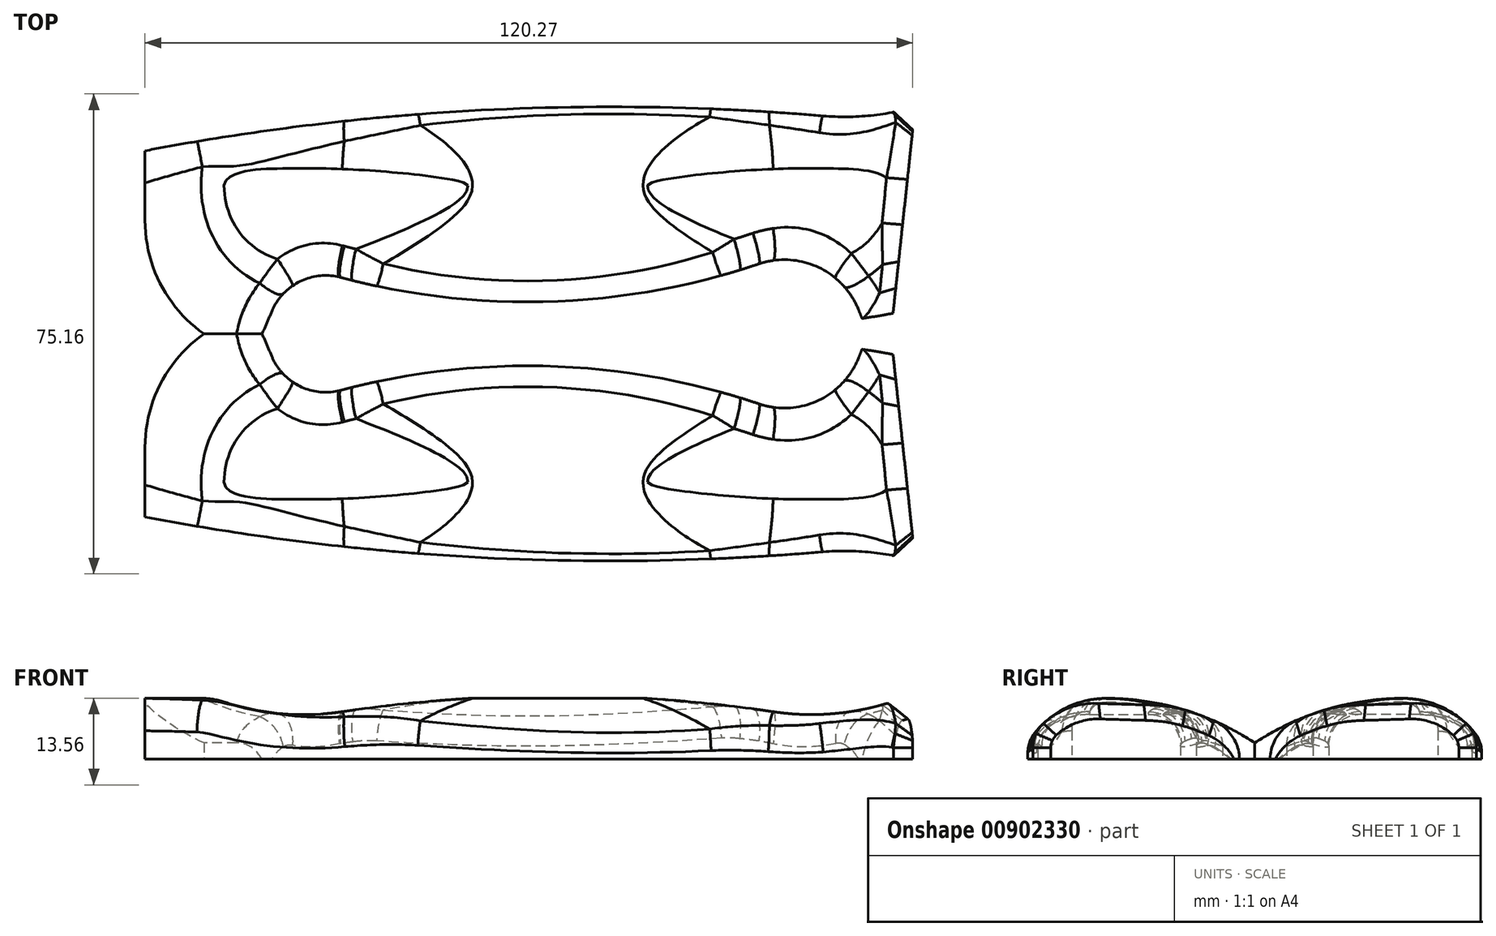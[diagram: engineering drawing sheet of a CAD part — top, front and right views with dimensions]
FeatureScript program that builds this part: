
annotation { "Feature Type Name" : "Feature", "Feature Type Description" : "" }
export const myFeature = defineFeature(function(context is Context, id is Id, definition is map)
    precondition{}
    {
        {
            var Q0;
            Q0=qCreatedBy(makeId("Top.planeOp"),FACE);
            var sketch = newSketch(context, id + "F0", { "sketchPlane" : qUnion([Q0])});
            skLineSegment(sketch, "E0", {"start": v(0, 35.56) * mm, "end": v(0, 0) * mm, "construction": true});
            skLineSegment(sketch, "E1", {"start": v(0, 0) * mm, "end": v(116.84, 0) * mm, "construction": true});
            skLineSegment(sketch, "E2", {"start": v(116.84, 0) * mm, "end": v(120.65, 35.56) * mm, "construction": true});
            skLineSegment(sketch, "E3", {"start": v(120.65, 35.56) * mm, "end": v(0, 35.56) * mm, "construction": true});
            skSolve(sketch);
        }
        {
            var Q0;
            Q0=qCreatedBy(makeId("Top.planeOp"),FACE);
            var sketch = newSketch(context, id + "F1", { "sketchPlane" : qUnion([Q0])});
            skLineSegment(sketch, "E4.0", {"start": v(120.65, 35.56) * mm, "end": v(0, 35.56) * mm, "construction": true});
            skLineSegment(sketch, "E5.0", {"start": v(0, 35.56) * mm, "end": v(0, 0) * mm, "construction": true});
            skLineSegment(sketch, "E6.0", {"start": v(0, 0) * mm, "end": v(116.84, 0) * mm, "construction": true});
            skLineSegment(sketch, "E7.0", {"start": v(116.84, 0) * mm, "end": v(120.65, 35.56) * mm, "construction": true});
            skArc(sketch, "E8", {"start": v(120.34, 32.66) * mm, "mid": v(113.28, 33.46) * mm, "end": v(106.21, 34.14) * mm, "construction": true});
            skArc(sketch, "E9", {"start": v(0, 17.78) * mm, "mid": v(2.44, 7.76) * mm, "end": v(9.23, 0) * mm});
            skLineSegment(sketch, "E10", {"start": v(0, 28.68) * mm, "end": v(0, 17.78) * mm});
            skArc(sketch, "E11", {"start": v(106.21, 34.14) * mm, "mid": v(113.5, 34.18) * mm, "end": v(120.65, 35.56) * mm});
            skArc(sketch, "E12", {"start": v(30.65, 8.84) * mm, "mid": v(22.72, 7.25) * mm, "end": v(19.15, 0) * mm});
            skArc(sketch, "E13", {"start": v(30.65, 8.84) * mm, "mid": v(63.56, 5.06) * mm, "end": v(96.16, 10.96) * mm});
            skArc(sketch, "E14", {"start": v(106.21, 34.14) * mm, "mid": v(52.92, 35.05) * mm, "end": v(0, 28.68) * mm});
            skLineSegment(sketch, "E15", {"start": v(120.65, 35.56) * mm, "end": v(116.84, 0) * mm});
            skLineSegment(sketch, "E16", {"start": v(112.65, 0) * mm, "end": v(116.84, 0) * mm});
            skArc(sketch, "E17", {"start": v(112.65, 0) * mm, "mid": v(107.1, 9.52) * mm, "end": v(96.16, 10.96) * mm});
            skLineSegment(sketch, "E18", {"start": v(9.23, 0) * mm, "end": v(19.15, 0) * mm});
            skSolve(sketch);
        }
        {
            var Q0;
            Q0 = qSketchRegion(id + "F1", true);
            extrude(context, id + "F2", {"entities" : qUnion([Q0]), "depth" : 12.7 * mm, "offsetDistance" : 25.4 * mm});
        }
        {
            var Q0;
            Q0=qCreatedBy(makeId("Right.planeOp"),FACE);
            var sketch = newSketch(context, id + "F3", { "sketchPlane" : qUnion([Q0])});
            skLineSegment(sketch, "E19.0", {"start": v(35.56, 0) * mm, "end": v(0, 0) * mm, "construction": true});
            skLineSegment(sketch, "E20", {"start": v(35.56, 0) * mm, "end": v(35.56, 2.54) * mm, "construction": true});
            skLineSegment(sketch, "E21", {"start": v(35.56, 2.54) * mm, "end": v(35.56, 2.54) * mm});
            skLineSegment(sketch, "E22", {"start": v(0, 2.54) * mm, "end": v(0, 0) * mm, "construction": true});
            skLineSegment(sketch, "E23", {"start": v(23.23, 12.7) * mm, "end": v(23.23, -4.85) * mm, "construction": true});
            skLineSegment(sketch, "E24", {"start": v(17.78, 12.7) * mm, "end": v(17.78, -21.71) * mm, "construction": true});
            skArc(sketch, "E25", {"start": v(23.23, 9.52) * mm, "mid": v(11.1, 7.74) * mm, "end": v(0, 2.54) * mm});
            skArc(sketch, "E26", {"start": v(0, 2.54) * mm, "mid": v(35.36, -72.92) * mm, "end": v(23.23, 9.52) * mm, "construction": true});
            skLineSegment(sketch, "E27", {"start": v(35.56, 2.54) * mm, "end": v(0, 2.54) * mm, "construction": true});
            skArc(sketch, "E28", {"start": v(23.23, 9.53) * mm, "mid": v(16.14, -17.36) * mm, "end": v(35.56, 2.54) * mm, "construction": true});
            skArc(sketch, "E29", {"start": v(35.56, 2.54) * mm, "mid": v(30.31, 7.66) * mm, "end": v(23.23, 9.53) * mm});
            skLineSegment(sketch, "E30.0", {"start": v(35.56, 12.7) * mm, "end": v(0, 12.7) * mm});
            skLineSegment(sketch, "E31", {"start": v(35.56, 2.54) * mm, "end": v(35.56, 12.7) * mm});
            skLineSegment(sketch, "E32", {"start": v(0, 12.7) * mm, "end": v(0, 2.54) * mm});
            skSolve(sketch);
        }
        {
            var Q0;
            Q0 = qSketchRegion(id + "F3", true);
            extrude(context, id + "F4", {"entities" : qUnion([Q0]), "operationType" : NewBodyOperationType.REMOVE, "endBound" : BoundingType.THROUGH_ALL, "depth" : 254 * mm, "offsetDistance" : 25.4 * mm});
        }
        {
            var Q0;
            Q0=qCreatedBy(makeId("Front.planeOp"),FACE);
            var sketch = newSketch(context, id + "F5", { "sketchPlane" : qUnion([Q0])});
            skLineSegment(sketch, "E33.0", {"start": v(30.65, 0) * mm, "end": v(19.15, 0) * mm, "construction": true});
            skLineSegment(sketch, "E34.0", {"start": v(112.65, 0) * mm, "end": v(96.16, 0) * mm, "construction": true});
            skLineSegment(sketch, "E35", {"start": v(24.9, 47.63) * mm, "end": v(24.9, 0) * mm, "construction": true});
            skLineSegment(sketch, "E36", {"start": v(104.4, 0) * mm, "end": v(104.4, 47.62) * mm, "construction": true});
            skLineSegment(sketch, "E37.0", {"start": v(119.33, 9.52) * mm, "end": v(118.55, 9.52) * mm});
            skArc(sketch, "E38", {"start": v(98.4, 7.43) * mm, "mid": v(64.65, 9.94) * mm, "end": v(30.9, 7.43) * mm});
            skArc(sketch, "E39", {"start": v(30.9, 7.43) * mm, "mid": v(61.28, -447.24) * mm, "end": v(105.07, 6.34) * mm, "construction": true});
            skArc(sketch, "E40", {"start": v(105.07, 6.34) * mm, "mid": v(101.74, 6.9) * mm, "end": v(98.4, 7.43) * mm});
            skLineSegment(sketch, "E41", {"start": v(118.55, 9.53) * mm, "end": v(10.76, 9.53) * mm, "construction": true});
            skLineSegment(sketch, "E42", {"start": v(119.33, 9.53) * mm, "end": v(10.76, 9.53) * mm});
            skArc(sketch, "E43", {"start": v(10.76, 9.53) * mm, "mid": v(20.7, 7.2) * mm, "end": v(30.9, 7.43) * mm});
            skArc(sketch, "E44", {"start": v(30.9, 7.43) * mm, "mid": v(29.1, 88.05) * mm, "end": v(10.76, 9.53) * mm, "construction": true});
            skArc(sketch, "E45", {"start": v(118.55, 9.52) * mm, "mid": v(100.2, 88.05) * mm, "end": v(98.4, 7.43) * mm, "construction": true});
            skArc(sketch, "E46", {"start": v(98.4, 7.43) * mm, "mid": v(108.61, 7.2) * mm, "end": v(118.55, 9.52) * mm});
            skLineSegment(sketch, "E47", {"start": v(119.33, 9.52) * mm, "end": v(119.33, 47.62) * mm});
            skLineSegment(sketch, "E48", {"start": v(119.33, 47.62) * mm, "end": v(119.33, 47.62) * mm});
            skSolve(sketch);
        }
        {
            var Q0;
            Q0 = qSketchRegion(id + "F5", true);
            extrude(context, id + "F6", {"entities" : qUnion([Q0]), "operationType" : NewBodyOperationType.REMOVE, "endBound" : BoundingType.THROUGH_ALL, "oppositeDirection" : true, "depth" : 101.6 * mm, "offsetDistance" : 25.4 * mm});
        }
        {
            var Q0;
            Q0=makeQuery(id+"F6.boolean.opBoolean","INTERSECT",EDGE,{"disambiguationData":[OD(1.0)],"derivedFrom":[makeQuery(id+"F4.boolean.opBoolean","COPY",FACE,{"derivedFrom":makeQuery(id+"F4.opExtrude","SWEPT_FACE",FACE,{"disambiguationData":[OSD([sQuery(id+"F3.wireOp",EDGE,"E25")])]})}),makeQuery(id+"F6.opExtrude","SWEPT_FACE",FACE,{"disambiguationData":[OSD([sQuery(id+"F5.wireOp",EDGE,"E43")])]})]});
            var Q1;
            Q1=makeQuery(id+"F6.boolean.opBoolean","INTERSECT",EDGE,{"disambiguationData":[OD(1.0)],"derivedFrom":[makeQuery(id+"F4.boolean.opBoolean","COPY",FACE,{"derivedFrom":makeQuery(id+"F4.opExtrude","SWEPT_FACE",FACE,{"disambiguationData":[OSD([sQuery(id+"F3.wireOp",EDGE,"E25")])]})}),makeQuery(id+"F6.opExtrude","SWEPT_FACE",FACE,{"disambiguationData":[OSD([sQuery(id+"F5.wireOp",EDGE,"E38")])]})]});
            fillet(context, id + "F7", {"entities" : qUnion([Q0, Q1]), "radius" : 11.68 * mm, "tangentPropagation" : true, "allowEdgeOverflow" : false});
        }
        {
            var Q0;
            Q0=makeQuery(id+"F4.boolean.opBoolean","INTERSECT",EDGE,{"derivedFrom":[makeQuery(id+"F2.opExtrude","SWEPT_FACE",FACE,{"disambiguationData":[OSD([sQuery(id+"F1.wireOp",EDGE,"E13")])]}),makeQuery(id+"F4.opExtrude","SWEPT_FACE",FACE,{"disambiguationData":[OSD([sQuery(id+"F3.wireOp",EDGE,"E25")])]})]});
            var Q1;
            Q1=makeQuery(id+"F4.boolean.opBoolean","INTERSECT",EDGE,{"derivedFrom":[makeQuery(id+"F2.opExtrude","SWEPT_FACE",FACE,{"disambiguationData":[OSD([sQuery(id+"F1.wireOp",EDGE,"E14")])]}),makeQuery(id+"F4.opExtrude","SWEPT_FACE",FACE,{"disambiguationData":[OSD([sQuery(id+"F3.wireOp",EDGE,"E29")])]})]});
            fillet(context, id + "F8", {"entities" : qUnion([Q0, Q1]), "radius" : 5.08 * mm, "tangentPropagation" : true, "allowEdgeOverflow" : false});
        }
        {
            var Q0;
            Q0=makeQuery(id+"F4.boolean.opBoolean","INTERSECT",EDGE,{"derivedFrom":[makeQuery(id+"F2.opExtrude","SWEPT_FACE",FACE,{"disambiguationData":[OSD([sQuery(id+"F1.wireOp",EDGE,"E15")])]}),makeQuery(id+"F4.opExtrude","SWEPT_FACE",FACE,{"disambiguationData":[OSD([sQuery(id+"F3.wireOp",EDGE,"E25")])]})]});
            var Q1;
            Q1=makeQuery(id+"F7.opFillet","BLEND_EDGE",EDGE,{"blendedFrom":[makeQuery(id+"F6.boolean.opBoolean","INTERSECT",EDGE,{"derivedFrom":[makeQuery(id+"F4.boolean.opBoolean","COPY",FACE,{"derivedFrom":makeQuery(id+"F4.opExtrude","SWEPT_FACE",FACE,{"disambiguationData":[OSD([sQuery(id+"F3.wireOp",EDGE,"E25")])]})}),makeQuery(id+"F6.opExtrude","SWEPT_FACE",FACE,{"disambiguationData":[OSD([sQuery(id+"F5.wireOp",EDGE,"E46")])]})]}),makeQuery(id+"F2.opExtrude","SWEPT_FACE",FACE,{"disambiguationData":[OSD([sQuery(id+"F1.wireOp",EDGE,"E15")])]})],"blendedInto":[makeQuery(id+"F2.opExtrude","SWEPT_FACE",FACE,{"disambiguationData":[OSD([sQuery(id+"F1.wireOp",EDGE,"E15")])]})]});
            chamfer(context, id + "F9", {"entities" : qUnion([Q0, Q1]), "width" : 2.54 * mm, "tangentPropagation" : true});
        }
        {
            var Q0;
            Q0=makeQuery(id+"F2.opExtrude","SWEPT_BODY",BODY,{"disambiguationData":[OSD([sQuery(id+"F1.wireOp",EDGE,"E9"),sQuery(id+"F1.wireOp",EDGE,"E10"),sQuery(id+"F1.wireOp",EDGE,"E11"),sQuery(id+"F1.wireOp",EDGE,"E12"),sQuery(id+"F1.wireOp",EDGE,"E13"),sQuery(id+"F1.wireOp",EDGE,"E14"),sQuery(id+"F1.wireOp",EDGE,"E15"),sQuery(id+"F1.wireOp",EDGE,"E16"),sQuery(id+"F1.wireOp",EDGE,"E17"),sQuery(id+"F1.wireOp",EDGE,"E18")])]});
            var Q1;
            Q1=qCreatedBy(makeId("Front.planeOp"),FACE);
            mirror(context, id + "F10", {"operationType" : NewBodyOperationType.ADD, "entities" : qUnion([Q0]), "mirrorPlane" : qUnion([Q1])});
        }
    });
